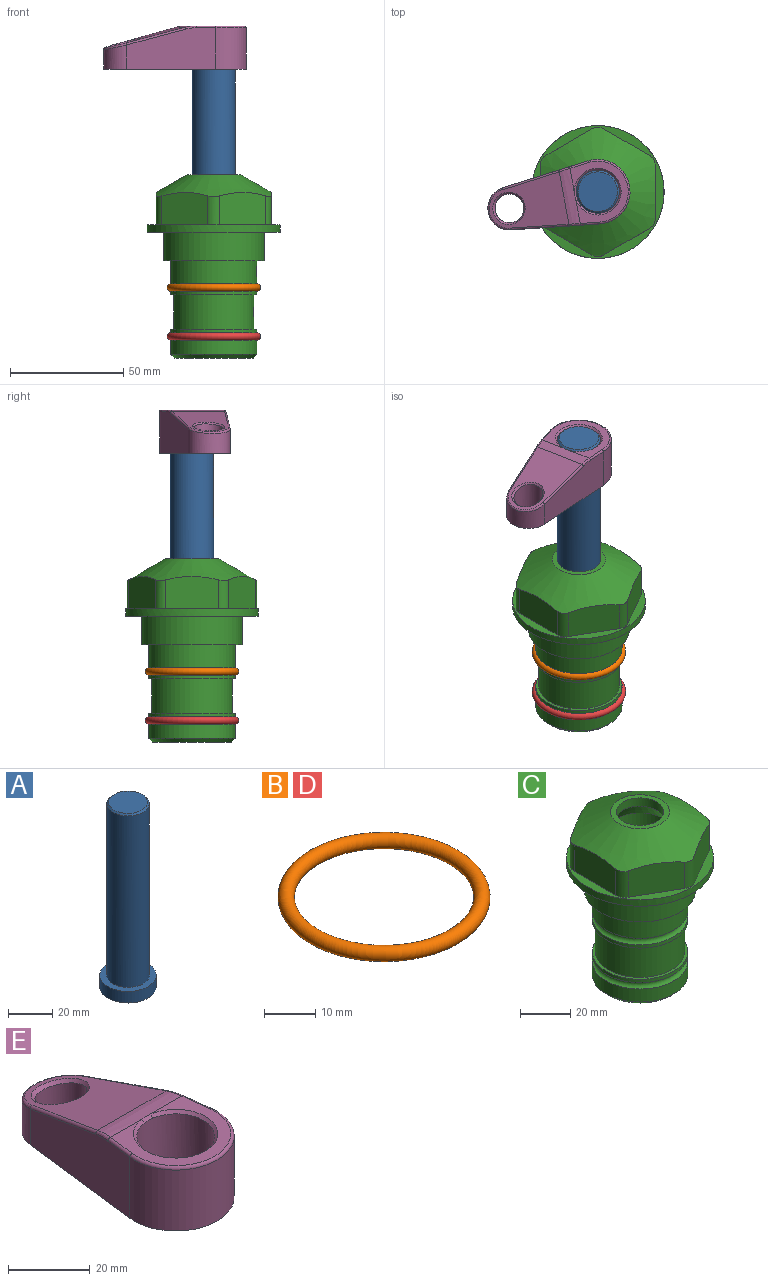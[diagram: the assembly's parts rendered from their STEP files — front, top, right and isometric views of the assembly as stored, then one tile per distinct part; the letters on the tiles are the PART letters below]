
ASSEMBLY  parts=5 mates=4
PART A: 6 faces, bbox 25.4x25.4x101.6 mm
  f0: plane 17.46x17.46mm, normal (0,0,1), area 239.5mm2, adj f5
  f1: plane 25.4x25.4mm, normal (0,0,-1), area 506.7mm2, adj f2
  f2: cylinder r=12.7mm len=25.4mm, axis (0,0,1), area 506.7mm2, adj f1,f3
  f3: plane 25.4x25.4mm, normal (0,0,1), area 221.7mm2, adj f2,f4
  f4: cylinder r=9.53mm len=94.46mm, axis (0,0,1), area 5653mm2, adj f3,f5
  f5: cone r=8.73mm half-angle=45deg, axis (0,0,-1), area 64.4mm2, adj f0,f4
PART B: 1 faces, bbox 44.7x44.7x3.2 mm
  f0: torus R=19.05mm, axis (0,0,1), area 1193.9mm2
PART C: 36 faces, bbox 58.7x58.7x81 mm
  f0: cylinder r=17.78mm len=35.56mm, axis (0,0,1), area 1670.8mm2, adj f23,f24,f31
  f1: cylinder r=19.05mm len=38.1mm, axis (0,0,1), area 1191.9mm2, adj f26,f27,f30
  f2: plane 58.66x58.66mm, normal (0,0,-1), area 1150.6mm2, adj f3,f28
  f3: cylinder r=29.33mm len=58.66mm, axis (0,0,-1), area 585.1mm2, adj f2,f4
  f4: plane 58.66x58.66mm, normal (0,0,1), area 475.9mm2, adj f3,f5,f6,f7,f8,f9,f10,f11
  f5: plane 20.32x14.34mm, normal (-0.5,0.87,0), area 324.4mm2, adj f4,f15,f16,f17
  f6: plane 20.32x14.34mm, normal (0.5,0.87,0), area 324.4mm2, adj f4,f14,f15,f17
  f7: plane 23.48x14.34mm, normal (1,0,0), area 324.4mm2, adj f4,f13,f14,f17
  f8: plane 20.32x14.34mm, normal (0.5,-0.87,0), area 324.4mm2, adj f4,f12,f13,f17
  f9: plane 20.32x14.34mm, normal (-0.5,-0.87,0), area 324.4mm2, adj f4,f11,f12,f17
  f10: plane 23.48x14.34mm, normal (-1,0,0), area 324.4mm2, adj f4,f11,f16,f17
  f11: cylinder r=5.08mm len=12.85mm, axis (0,0,-1), area 67.2mm2, adj f4,f9,f10,f17
  f12: cylinder r=5.08mm len=12.85mm, axis (0,0,-1), area 67.2mm2, adj f4,f8,f9,f17
  f13: cylinder r=5.08mm len=12.85mm, axis (0,0,-1), area 67.2mm2, adj f4,f7,f8,f17
  f14: cylinder r=5.08mm len=12.85mm, axis (0,0,-1), area 67.2mm2, adj f4,f6,f7,f17
  f15: cylinder r=5.08mm len=12.85mm, axis (0,0,-1), area 67.2mm2, adj f4,f5,f6,f17
  f16: cylinder r=5.08mm len=12.85mm, axis (0,0,-1), area 67.2mm2, adj f4,f5,f10,f17
  f17: cone r=11.73mm half-angle=60deg, axis (0,0,-1), area 2071.8mm2, adj f5,f6,f7,f8,f9,f10,f11,f12
  f18: plane 23.46x23.46mm, normal (0,0,1), area 147.4mm2, adj f17,f35
  f19: plane 34.93x34.93mm, normal (0,0,-1), area 958mm2, adj f29
  f20: cylinder r=19.05mm len=38.1mm, axis (0,0,1), area 760.1mm2, adj f21,f29
  f21: torus R=19.05mm, axis (0,0,1), area 565.3mm2, adj f20,f22
  f22: cylinder r=19.05mm len=38.1mm, axis (0,0,1), area 190mm2, adj f21,f23
  f23: plane 38.1x38.1mm, normal (0,0,1), area 146.9mm2, adj f0,f22
  f24: plane 38.1x38.1mm, normal (0,0,-1), area 146.9mm2, adj f0,f25
  f25: cylinder r=19.05mm len=38.1mm, axis (0,0,1), area 190mm2, adj f24,f26
  f26: torus R=19.05mm, axis (0,0,1), area 565.3mm2, adj f1,f25
  f27: plane 44.45x44.45mm, normal (0,0,-1), area 411.7mm2, adj f1,f28
  f28: cylinder r=22.23mm len=44.45mm, axis (0,0,1), area 1773.5mm2, adj f2,f27
  f29: cone r=19.05mm half-angle=45deg, axis (0,0,1), area 257.5mm2, adj f19,f20
  f30: cylinder r=3.17mm len=6.75mm, axis (-1,0,0), area 128mm2, adj f1,f33
  f31: cylinder r=3.17mm len=6.35mm, axis (-1,0,0), area 102.5mm2, adj f0,f33
  f32: plane 25.4x25.4mm, normal (0,0,1), area 506.7mm2, adj f33
  f33: cylinder r=12.7mm len=66.42mm, axis (0,0,-1), area 5236.2mm2, adj f30,f31,f32,f34
  f34: cone r=9.53mm half-angle=30deg, axis (0,0,-1), area 443.4mm2, adj f33,f35
  f35: cylinder r=9.53mm len=19.05mm, axis (0,0,-1), area 240.9mm2, adj f18,f34
PART D: same geometry as B
PART E: 31 faces, bbox 31.7x65.5x19.8 mm
  f0: plane 39.12x18.26mm, normal (0.99,0.12,0), area 612.2mm2, adj f1,f4,f7,f11,f13,f15
  f1: cylinder r=9.53mm len=18.91mm, axis (0,0,-1), area 296.1mm2, adj f0,f2,f7,f17
  f2: plane 39.12x18.26mm, normal (-0.99,0.12,0), area 612.2mm2, adj f1,f4,f7,f12,f14,f16
  f3: cylinder r=6.35mm len=12.7mm, axis (0,0,-1), area 362.4mm2, adj f7,f18
  f4: cylinder r=14.29mm len=28.58mm, axis (0,0,-1), area 882.2mm2, adj f0,f2,f7,f10
  f5: cylinder r=9.53mm len=19.05mm, axis (0,0,-1), area 1092.6mm2, adj f7,f19,f20
  f6: plane 26.99x23.69mm, normal (0,0,1), area 216.2mm2, adj f9,f10,f11,f12,f19
  f7: plane 63.5x28.58mm, normal (0,0,-1), area 661.8mm2, adj f0,f1,f2,f3,f4,f5,f22,f23
  f8: plane 33.52x23.6mm, normal (0,0.26,0.97), area 486mm2, adj f9,f15,f16,f17,f18
  f9: cylinder r=19.05mm len=24.72mm, axis (1,0,0), area 120.4mm2, adj f6,f8,f13,f14,f20
  f10: torus R=13.49mm, axis (0,0,1), area 59mm2, adj f4,f6,f11,f12
  f11: cylinder r=0.79mm len=8.67mm, axis (0.12,-0.99,0), area 10.8mm2, adj f0,f6,f10,f13
  f12: cylinder r=0.79mm len=8.67mm, axis (0.12,0.99,0), area 10.8mm2, adj f2,f6,f10,f14
  f13: bspline ~4.95x1.42mm, area 6.1mm2, adj f0,f9,f11,f15
  f14: bspline ~4.95x1.42mm, area 6.1mm2, adj f2,f9,f12,f16
  f15: cylinder r=0.79mm len=25.95mm, axis (0.12,-0.96,0.26), area 32.9mm2, adj f0,f8,f13,f17
  f16: cylinder r=0.79mm len=25.95mm, axis (0.12,0.96,-0.26), area 32.9mm2, adj f2,f8,f14,f17
  f17: bspline ~18.91x8.38mm, area 30mm2, adj f1,f8,f15,f16
  f18: bspline ~14.29x14.29mm, area 48.3mm2, adj f3,f8
  f19: cone r=9.53mm half-angle=45deg, axis (0,0,1), area 66.5mm2, adj f5,f6,f20
  f20: bspline ~3.22x0.96mm, area 3.5mm2, adj f5,f9,f19
  f21: plane 2.75x2.72mm, normal (0,0,-1), area 2.9mm2, adj f23,f25,f28
  f22: plane 23.05x15.88mm, normal (-0.99,-0.12,0), area 323.6mm2, adj f7,f25,f26,f27,f28,f29
  f23: plane 23.05x15.88mm, normal (0.99,-0.12,0), area 323.6mm2, adj f7,f21,f25,f27,f28,f30
  f24: cylinder r=9.53mm len=10.69mm, axis (0,0,-1), area 114.7mm2, adj f7,f27,f29,f30
  f25: cylinder r=12.7mm len=20.59mm, axis (0,0,-1), area 381.1mm2, adj f7,f21,f22,f23,f26,f28
  f26: plane 2.75x2.72mm, normal (0,0,-1), area 2.9mm2, adj f22,f25,f28
  f27: plane 19.72x18.37mm, normal (0,-0.26,-0.97), area 291.8mm2, adj f22,f23,f24,f28,f29,f30
  f28: cylinder r=15.88mm len=19.92mm, axis (1,0,0), area 54.8mm2, adj f21,f22,f23,f25,f26,f27
  f29: cylinder r=1.59mm len=11mm, axis (0,0,-1), area 34.7mm2, adj f7,f22,f24,f27
  f30: cylinder r=1.59mm len=11mm, axis (0,0,-1), area 34.7mm2, adj f7,f23,f24,f27
PLACE A rot(axis=(0,0,1),100.7deg) t=(0,0,27.55)mm
PLACE B at identity
PLACE C at identity fixed
PLACE D t=(0,0,-21.59)mm
PLACE E rot(axis=(0,0,1),100.7deg) t=(0,0,27.55)mm
MATE cylindrical A.f2 <-> C.f0  axis (0,0,-1) through (0,0,-10.55)mm
MATE fastened A.f2 <-> E.f4  axis (0,0,1) through (0,0,91.05)mm
MATE fastened B.f0 <-> C.f0  axis (0,0,1) through (0,0,-24.51)mm
MATE fastened D.f0 <-> C.f0  axis (0,0,1) through (0,0,-46.1)mm
